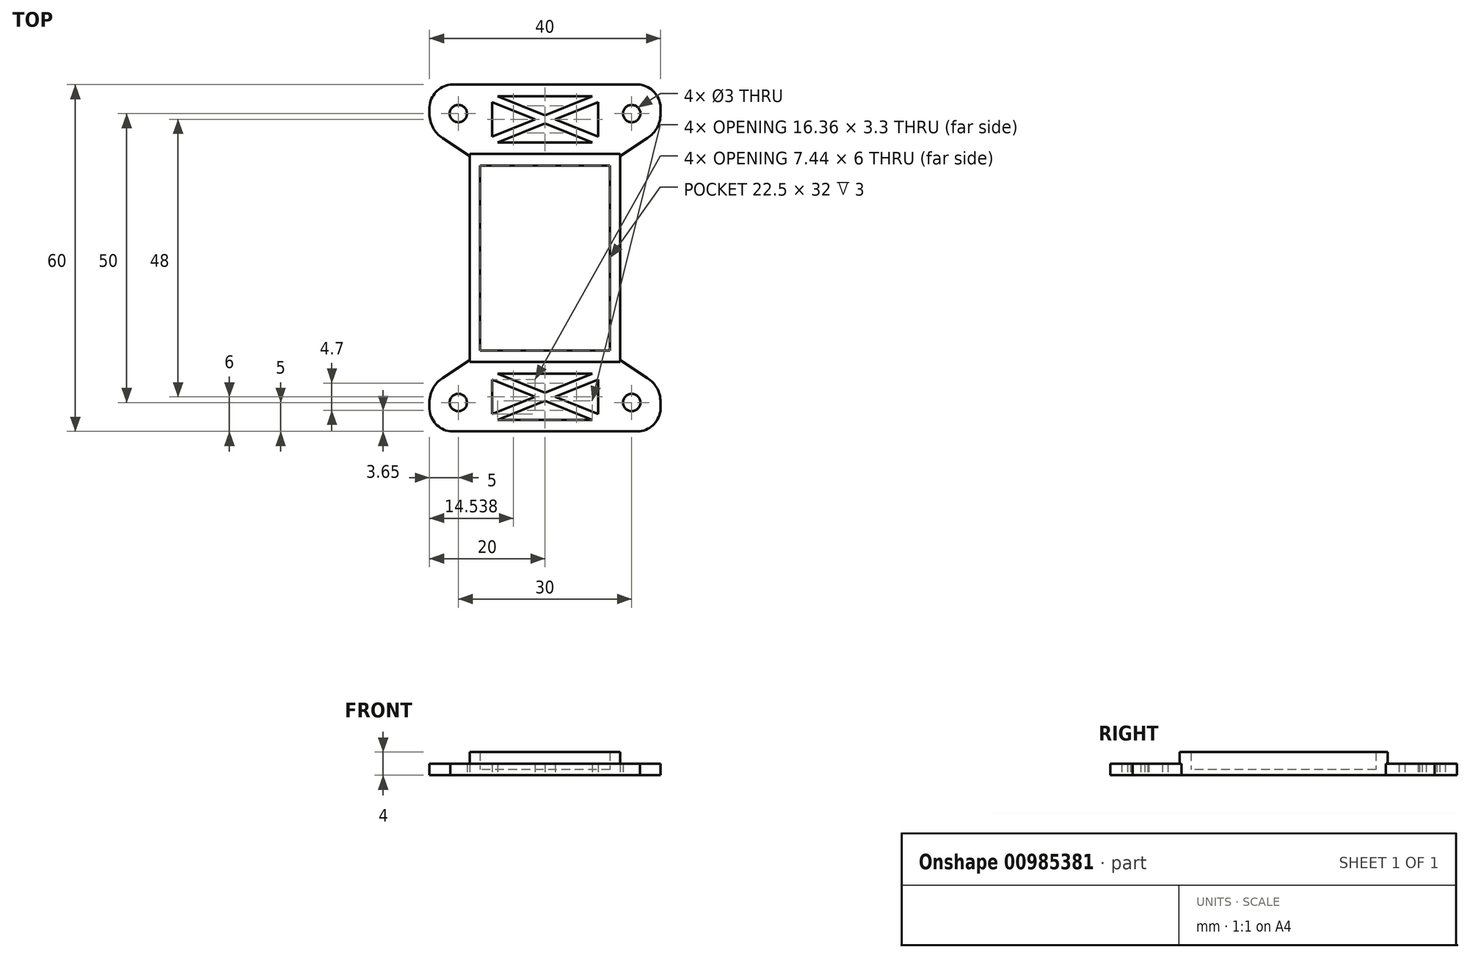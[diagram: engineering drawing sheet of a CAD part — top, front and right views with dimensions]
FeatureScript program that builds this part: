
annotation { "Feature Type Name" : "Feature", "Feature Type Description" : "" }
export const myFeature = defineFeature(function(context is Context, id is Id, definition is map)
    precondition{}
    {
        {
            var Q0;
            Q0=qCreatedBy(makeId("Top.planeOp"),FACE);
            var sketch = newSketch(context, id + "F0", { "sketchPlane" : qUnion([Q0])});
            skLineSegment(sketch, "E0.bottom", {"start": v(16.4, 30) * mm, "end": v(-16.4, 30) * mm});
            skLineSegment(sketch, "E0.top", {"start": v(16.4, -30) * mm, "end": v(-16.4, -30) * mm});
            skLineSegment(sketch, "E0.left", {"start": v(20, 26.11) * mm, "end": v(20, 24.94) * mm});
            skLineSegment(sketch, "E0.right", {"start": v(-20, 26.11) * mm, "end": v(-20, 24.94) * mm});
            skPoint(sketch, "E0.middle", {"position": v(0, 0) * mm});
            skLineSegment(sketch, "E1.bottom", {"start": v(11.25, 16) * mm, "end": v(-11.25, 16) * mm});
            skLineSegment(sketch, "E1.top", {"start": v(11.25, -16) * mm, "end": v(-11.25, -16) * mm});
            skLineSegment(sketch, "E1.left", {"start": v(11.25, 16) * mm, "end": v(11.25, -16) * mm});
            skLineSegment(sketch, "E1.right", {"start": v(-11.25, 16) * mm, "end": v(-11.25, -16) * mm});
            skLineSegment(sketch, "E2.bottom", {"start": v(15, 25) * mm, "end": v(-15, 25) * mm, "construction": true});
            skLineSegment(sketch, "E2.top", {"start": v(15, -25) * mm, "end": v(-15, -25) * mm, "construction": true});
            skLineSegment(sketch, "E2.left", {"start": v(15, 25) * mm, "end": v(15, -25) * mm, "construction": true});
            skLineSegment(sketch, "E2.right", {"start": v(-15, 25) * mm, "end": v(-15, -25) * mm, "construction": true});
            skCircle(sketch, "E3", {"center": v(-15, 25) * mm, "radius": 1.5 * mm});
            skCircle(sketch, "E4", {"center": v(15, 25) * mm, "radius": 1.5 * mm});
            skCircle(sketch, "E5", {"center": v(15, -25) * mm, "radius": 1.5 * mm});
            skCircle(sketch, "E6", {"center": v(-15, -25) * mm, "radius": 1.5 * mm});
            skCircle(sketch, "E7", {"center": v(-15, 25) * mm, "radius": 3.5 * mm});
            skCircle(sketch, "E8", {"center": v(15, 25) * mm, "radius": 3.5 * mm});
            skCircle(sketch, "E9", {"center": v(15, -25) * mm, "radius": 3.5 * mm});
            skCircle(sketch, "E10", {"center": v(-15, -25) * mm, "radius": 3.5 * mm});
            skPoint(sketch, "E11.MirrorCS.end.orphan", {"position": v(-20.41, 25) * mm});
            skPoint(sketch, "E11.MirrorCS.start.orphan", {"position": v(-20, 22.34) * mm});
            skPoint(sketch, "E12.end.orphan", {"position": v(20.41, 25) * mm});
            skPoint(sketch, "E12.start.orphan", {"position": v(20, 22.34) * mm});
            skPoint(sketch, "E13.MirrorCS.end.orphan", {"position": v(20.41, -25) * mm});
            skPoint(sketch, "E13.MirrorCS.start.orphan", {"position": v(20, -22.34) * mm});
            skPoint(sketch, "E14.MirrorCS.end.orphan", {"position": v(-20.41, -25) * mm});
            skPoint(sketch, "E14.MirrorCS.start.orphan", {"position": v(-20, -22.34) * mm});
            skLineSegment(sketch, "E15", {"start": v(-17.73, 20.75) * mm, "end": v(-13, 17.67) * mm});
            skLineSegment(sketch, "E16.MirrorCS", {"start": v(-17.73, -20.75) * mm, "end": v(-13, -17.67) * mm});
            skLineSegment(sketch, "E17.MirrorCS", {"start": v(17.73, -20.75) * mm, "end": v(13, -17.67) * mm});
            skLineSegment(sketch, "E18.MirrorCS", {"start": v(17.73, 20.75) * mm, "end": v(13, 17.67) * mm});
            skLineSegment(sketch, "E19.trimOffspring", {"start": v(20, -24.94) * mm, "end": v(20, -26.11) * mm});
            skLineSegment(sketch, "E20.trimOffspring", {"start": v(-20, -24.94) * mm, "end": v(-20, -26.11) * mm});
            skArc(sketch, "E21", {"start": v(-16.4, 30) * mm, "mid": v(-18.9, 28.7) * mm, "end": v(-20, 26.11) * mm});
            skArc(sketch, "E22.MirrorCS", {"start": v(16.4, 30) * mm, "mid": v(18.9, 28.7) * mm, "end": v(20, 26.11) * mm});
            skArc(sketch, "E23.MirrorCS", {"start": v(16.4, -30) * mm, "mid": v(18.9, -28.7) * mm, "end": v(20, -26.11) * mm});
            skArc(sketch, "E24.MirrorCS", {"start": v(-16.4, -30) * mm, "mid": v(-18.9, -28.7) * mm, "end": v(-20, -26.11) * mm});
            skPoint(sketch, "E25.visualSharp", {"position": v(-20, -22.23) * mm});
            skArc(sketch, "E25.filletArc", {"start": v(-17.73, -20.75) * mm, "mid": v(-19.4, -22.56) * mm, "end": v(-20, -24.94) * mm});
            skPoint(sketch, "E26.visualSharp", {"position": v(20, -22.23) * mm});
            skArc(sketch, "E26.filletArc", {"start": v(20, -24.94) * mm, "mid": v(19.4, -22.56) * mm, "end": v(17.73, -20.75) * mm});
            skPoint(sketch, "E27.visualSharp", {"position": v(20, 22.23) * mm});
            skArc(sketch, "E27.filletArc", {"start": v(17.73, 20.75) * mm, "mid": v(19.4, 22.56) * mm, "end": v(20, 24.94) * mm});
            skPoint(sketch, "E28.visualSharp", {"position": v(-20, 22.23) * mm});
            skArc(sketch, "E28.filletArc", {"start": v(-20, 24.94) * mm, "mid": v(-19.4, 22.56) * mm, "end": v(-17.73, 20.75) * mm});
            skPoint(sketch, "E29.orphan", {"position": v(-20, 30) * mm});
            skPoint(sketch, "E30.orphan", {"position": v(20, 30) * mm});
            skPoint(sketch, "E31.orphan", {"position": v(20, -30) * mm});
            skPoint(sketch, "E32.orphan", {"position": v(-20, -30) * mm});
            skLineSegment(sketch, "E33.bottom", {"start": v(13, 18) * mm, "end": v(-13, 18) * mm});
            skLineSegment(sketch, "E33.top", {"start": v(13, -18) * mm, "end": v(-13, -18) * mm});
            skLineSegment(sketch, "E33.left", {"start": v(13, 18) * mm, "end": v(13, -18) * mm});
            skLineSegment(sketch, "E33.right", {"start": v(-13, 18) * mm, "end": v(-13, -18) * mm});
            skPoint(sketch, "E34.orphan", {"position": v(-11.25, 16.52) * mm});
            skPoint(sketch, "E35.orphan", {"position": v(11.25, 16.52) * mm});
            skPoint(sketch, "E36.orphan", {"position": v(11.25, -16.52) * mm});
            skPoint(sketch, "E37.orphan", {"position": v(-11.25, -16.52) * mm});
            skLineSegment(sketch, "E38.bottom", {"start": v(-9.18, 28) * mm, "end": v(9.17, 28) * mm});
            skLineSegment(sketch, "E38.top", {"start": v(-9.18, 20) * mm, "end": v(9.17, 20) * mm});
            skLineSegment(sketch, "E38.left", {"start": v(-9.18, 28) * mm, "end": v(-9.18, 20) * mm});
            skLineSegment(sketch, "E38.right", {"start": v(9.17, 28) * mm, "end": v(9.17, 20) * mm});
            skLineSegment(sketch, "E39", {"start": v(9.17, 21) * mm, "end": v(1.73, 24) * mm});
            skLineSegment(sketch, "E40", {"start": v(-8.18, 20) * mm, "end": v(0, 23.3) * mm});
            skLineSegment(sketch, "E41.MirrorCS", {"start": v(8.18, 20) * mm, "end": v(0, 23.3) * mm});
            skLineSegment(sketch, "E42.trimOffspring", {"start": v(1.73, 24) * mm, "end": v(9.17, 27) * mm});
            skLineSegment(sketch, "E43.trimOffspring", {"start": v(0, 24.7) * mm, "end": v(-8.18, 28) * mm});
            skLineSegment(sketch, "E44.trimOffspring", {"start": v(0, 24.7) * mm, "end": v(8.18, 28) * mm});
            skLineSegment(sketch, "E45", {"start": v(-9.18, 21) * mm, "end": v(-1.74, 24) * mm});
            skLineSegment(sketch, "E46", {"start": v(-1.74, 24) * mm, "end": v(-9.18, 27) * mm});
            skLineSegment(sketch, "E47.MirrorCS", {"start": v(8.18, -20) * mm, "end": v(0, -23.3) * mm});
            skLineSegment(sketch, "E48.MirrorCS", {"start": v(9.17, -21) * mm, "end": v(1.73, -24) * mm});
            skLineSegment(sketch, "E49.MirrorCS", {"start": v(1.73, -24) * mm, "end": v(9.17, -27) * mm});
            skLineSegment(sketch, "E50.MirrorCS", {"start": v(0, -24.7) * mm, "end": v(8.18, -28) * mm});
            skLineSegment(sketch, "E51.MirrorCS", {"start": v(0, -24.7) * mm, "end": v(-8.18, -28) * mm});
            skLineSegment(sketch, "E52.MirrorCS", {"start": v(-1.74, -24) * mm, "end": v(-9.18, -27) * mm});
            skLineSegment(sketch, "E53.MirrorCS", {"start": v(-8.18, -20) * mm, "end": v(0, -23.3) * mm});
            skLineSegment(sketch, "E54.MirrorCS", {"start": v(-9.18, -21) * mm, "end": v(-1.74, -24) * mm});
            skLineSegment(sketch, "E55.MirrorCS", {"start": v(9.17, -28) * mm, "end": v(9.17, -20) * mm});
            skLineSegment(sketch, "E56.MirrorCS", {"start": v(-9.18, -20) * mm, "end": v(9.17, -20) * mm});
            skLineSegment(sketch, "E57.MirrorCS", {"start": v(-9.18, -28) * mm, "end": v(-9.18, -20) * mm});
            skLineSegment(sketch, "E58.MirrorCS", {"start": v(-9.18, -28) * mm, "end": v(9.17, -28) * mm});
            skSolve(sketch);
        }
        {
            var Q0;
            Q0=makeQuery(id+"F0.imprint","IMPRINT",FACE,{"disambiguationData":[TD([[makeQuery(id+"F0.imprint","IMPRINT",EDGE,{"derivedFrom":sQuery(id+"F0.wireOp",EDGE,"E0.bottom")}),1.0]])]});
            var Q1;
            Q1=makeQuery(id+"F0.imprint","IMPRINT",FACE,{"disambiguationData":[TD([[makeQuery(id+"F0.imprint","IMPRINT",EDGE,{"derivedFrom":sQuery(id+"F0.wireOp",EDGE,"E0.top")}),-1.0]])]});
            var Q2;
            Q2=makeQuery(id+"F0.imprint","IMPRINT",FACE,{"disambiguationData":[TD([[makeQuery(id+"F0.imprint","IMPRINT",EDGE,{"derivedFrom":sQuery(id+"F0.wireOp",EDGE,"E6")}),-1.0]])]});
            var Q3;
            Q3=makeQuery(id+"F0.imprint","IMPRINT",FACE,{"disambiguationData":[TD([[makeQuery(id+"F0.imprint","IMPRINT",EDGE,{"derivedFrom":sQuery(id+"F0.wireOp",EDGE,"E5")}),-1.0]])]});
            var Q4;
            Q4=makeQuery(id+"F0.imprint","IMPRINT",FACE,{"disambiguationData":[TD([[makeQuery(id+"F0.imprint","IMPRINT",EDGE,{"derivedFrom":sQuery(id+"F0.wireOp",EDGE,"E4")}),-1.0]])]});
            var Q5;
            Q5=makeQuery(id+"F0.imprint","IMPRINT",FACE,{"disambiguationData":[TD([[makeQuery(id+"F0.imprint","IMPRINT",EDGE,{"derivedFrom":sQuery(id+"F0.wireOp",EDGE,"E3")}),-1.0]])]});
            var Q6;
            {var subQ0=sQuery(id+"F0.wireOp",EDGE,"E40");Q6=makeQuery(id+"F0.imprint","IMPRINT",FACE,{"disambiguationData":[TD([[makeQuery(id+"F0.imprint","IMPRINT",EDGE,{"derivedFrom":subQ0}),1.0]])]});}
            var Q7;
            {var subQ11=sQuery(id+"F0.wireOp",EDGE,"E47.MirrorCS");Q7=makeQuery(id+"F0.imprint","IMPRINT",FACE,{"disambiguationData":[TD([[makeQuery(id+"F0.imprint","IMPRINT",EDGE,{"derivedFrom":subQ11}),1.0]])]});}
            extrude(context, id + "F1", {"entities" : qUnion([Q0, Q1, Q2, Q3, Q4, Q5, Q6, Q7]), "depth" : 2 * mm, "offsetDistance" : 25 * mm});
        }
        {
            var Q0;
            Q0=makeQuery(id+"F0.imprint","IMPRINT",FACE,{"disambiguationData":[TD([[makeQuery(id+"F0.imprint","IMPRINT",EDGE,{"derivedFrom":sQuery(id+"F0.wireOp",EDGE,"E1.bottom")}),-1.0]])]});
            extrude(context, id + "F2", {"entities" : qUnion([Q0]), "operationType" : NewBodyOperationType.ADD, "depth" : 4 * mm, "offsetDistance" : 25 * mm});
        }
        {
            var Q0;
            Q0=makeQuery(id+"F0.imprint","IMPRINT",FACE,{"disambiguationData":[TD([[makeQuery(id+"F0.imprint","IMPRINT",EDGE,{"derivedFrom":sQuery(id+"F0.wireOp",EDGE,"E1.bottom")}),1.0]])]});
            extrude(context, id + "F3", {"entities" : qUnion([Q0]), "operationType" : NewBodyOperationType.ADD, "depth" : 1 * mm, "offsetDistance" : 25 * mm});
        }
    });
